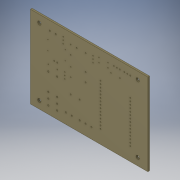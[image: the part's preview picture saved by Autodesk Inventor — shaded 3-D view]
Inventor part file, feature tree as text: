
AUTODESK INVENTOR PART (.ipt)
format: ipt  version: 2019 (Build 230136000, 136)  size: 295,424 bytes
history: native  units: mm
features: other x1, extrude x1, sketch x1, projected_geometry x1
ambient origin geometry x8: Origin, YZ Plane, XZ Plane, XY Plane, X Axis, Y Axis, Z Axis, Center Point
bodies: Solid1 (feature_tree)
feature tree (4):
  other  "Board"
  extrude  "Extrusion1"  [1 undecoded]
  sketch  "Sketch1"  dims[d0=0.12mm d1=0.0mm]
  projected_geometry  "Projected Loop1"
note: 1 required parameter value undecoded (feature->parameter linkage not recoverable at this tier; creation-order binding heuristic only, values carry confidence <= 0.55)
